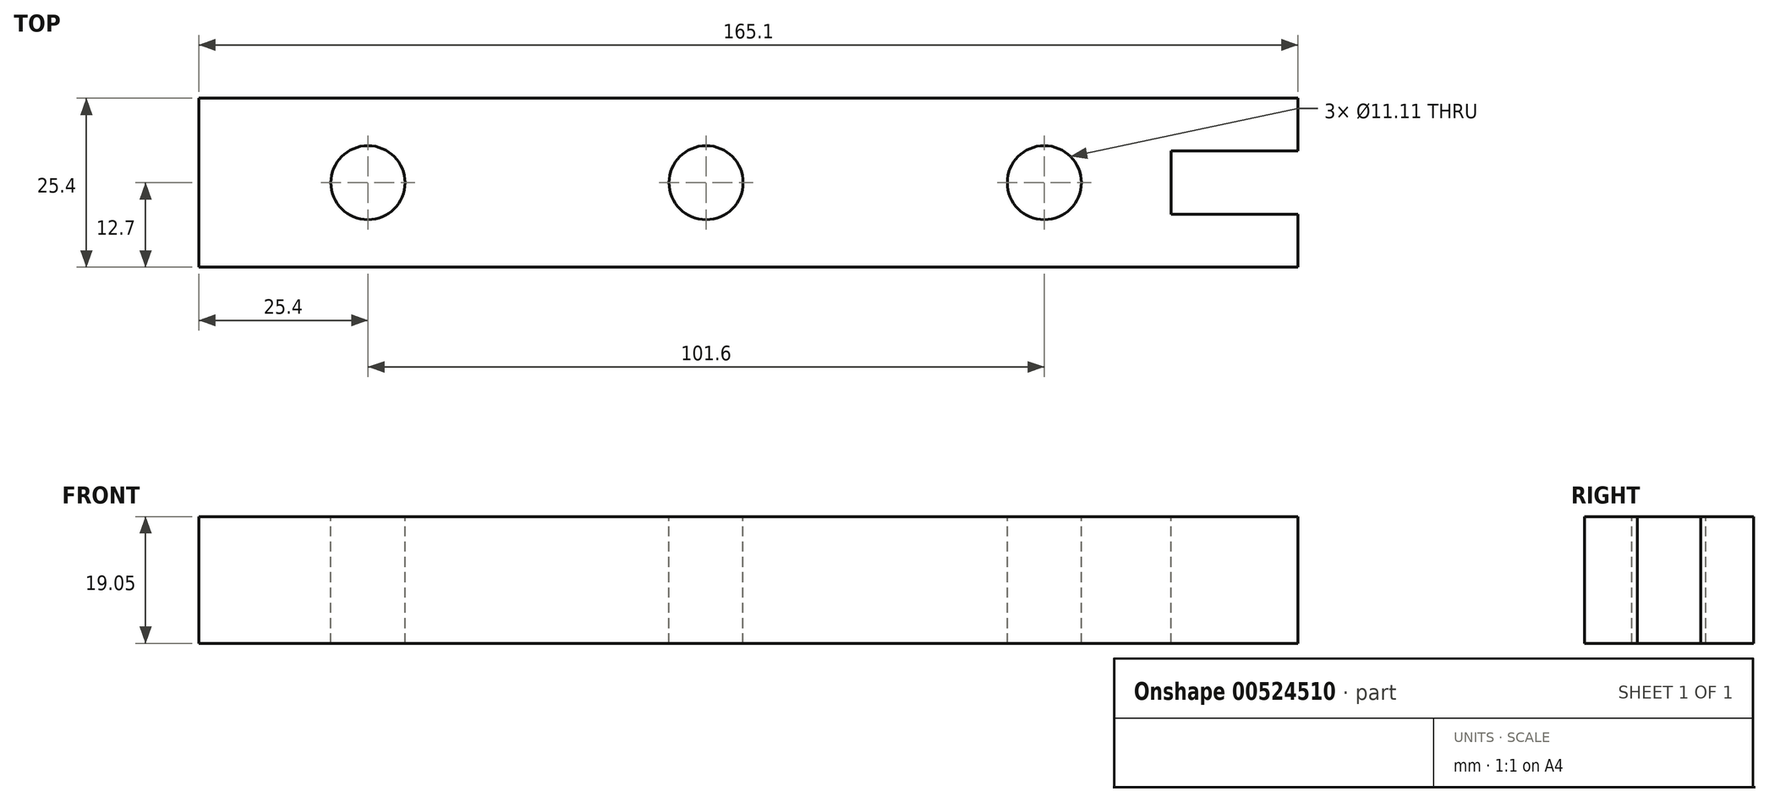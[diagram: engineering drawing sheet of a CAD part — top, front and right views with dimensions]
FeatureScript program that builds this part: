
annotation { "Feature Type Name" : "Feature", "Feature Type Description" : "" }
export const myFeature = defineFeature(function(context is Context, id is Id, definition is map)
    precondition{}
    {
        {
            var Q0;
            Q0=qCreatedBy(makeId("Top.planeOp"),FACE);
            var sketch = newSketch(context, id + "F0", { "sketchPlane" : qUnion([Q0])});
            skLineSegment(sketch, "E0.bottom", {"start": v(82.55, -12.7) * mm, "end": v(-82.55, -12.7) * mm});
            skLineSegment(sketch, "E0.top", {"start": v(82.55, 12.7) * mm, "end": v(-82.55, 12.7) * mm});
            skLineSegment(sketch, "E0.left", {"start": v(82.55, -12.7) * mm, "end": v(82.55, 12.7) * mm});
            skLineSegment(sketch, "E0.right", {"start": v(-82.55, -12.7) * mm, "end": v(-82.55, 12.7) * mm});
            skPoint(sketch, "E0.middle", {"position": v(0, 0) * mm});
            skSolve(sketch);
        }
        {
            var Q0;
            Q0 = qSketchRegion(id + "F0", true);
            extrude(context, id + "F1", {"entities" : qUnion([Q0]), "depth" : 19.05 * mm, "offsetDistance" : 25.4 * mm});
        }
        {
            var Q0;
            Q0=makeQuery(id+"F1.opExtrude","CAP_FACE",FACE,{"disambiguationData":[OSD([sQuery(id+"F0.wireOp",EDGE,"E0.bottom"),sQuery(id+"F0.wireOp",EDGE,"E0.top"),sQuery(id+"F0.wireOp",EDGE,"E0.left"),sQuery(id+"F0.wireOp",EDGE,"E0.right")])],"isStart":false});
            var sketch = newSketch(context, id + "F2", { "sketchPlane" : qUnion([Q0])});
            skLineSegment(sketch, "E1.bottom", {"start": v(82.55, -4.76) * mm, "end": v(63.5, -4.76) * mm});
            skLineSegment(sketch, "E1.top", {"start": v(82.55, 4.76) * mm, "end": v(63.5, 4.76) * mm});
            skLineSegment(sketch, "E1.left", {"start": v(82.55, -4.76) * mm, "end": v(82.55, 4.76) * mm});
            skLineSegment(sketch, "E1.right", {"start": v(63.5, -4.76) * mm, "end": v(63.5, 4.76) * mm});
            skPoint(sketch, "E1.middle", {"position": v(73.03, 0) * mm});
            skSolve(sketch);
        }
        {
            var Q0;
            Q0 = qSketchRegion(id + "F2", true);
            extrude(context, id + "F3", {"entities" : qUnion([Q0]), "operationType" : NewBodyOperationType.REMOVE, "endBound" : BoundingType.THROUGH_ALL, "oppositeDirection" : true, "depth" : 25.4 * mm, "offsetDistance" : 25.4 * mm});
        }
        {
            var Q0;
            Q0=makeQuery(id+"F1.opExtrude","CAP_FACE",FACE,{"disambiguationData":[OSD([sQuery(id+"F0.wireOp",EDGE,"E0.bottom"),sQuery(id+"F0.wireOp",EDGE,"E0.top"),sQuery(id+"F0.wireOp",EDGE,"E0.left"),sQuery(id+"F0.wireOp",EDGE,"E0.right")])],"isStart":false});
            var sketch = newSketch(context, id + "F4", { "sketchPlane" : qUnion([Q0])});
            skCircle(sketch, "E2", {"center": v(-57.15, 0) * mm, "radius": 5.56 * mm});
            skCircle(sketch, "E3", {"center": v(-6.35, 0) * mm, "radius": 5.56 * mm});
            skCircle(sketch, "E4", {"center": v(44.45, 0) * mm, "radius": 5.56 * mm});
            skSolve(sketch);
        }
        {
            var Q0;
            Q0 = qSketchRegion(id + "F4", true);
            extrude(context, id + "F5", {"entities" : qUnion([Q0]), "operationType" : NewBodyOperationType.REMOVE, "endBound" : BoundingType.THROUGH_ALL, "oppositeDirection" : true, "depth" : 25.4 * mm, "offsetDistance" : 25.4 * mm});
        }
    });
